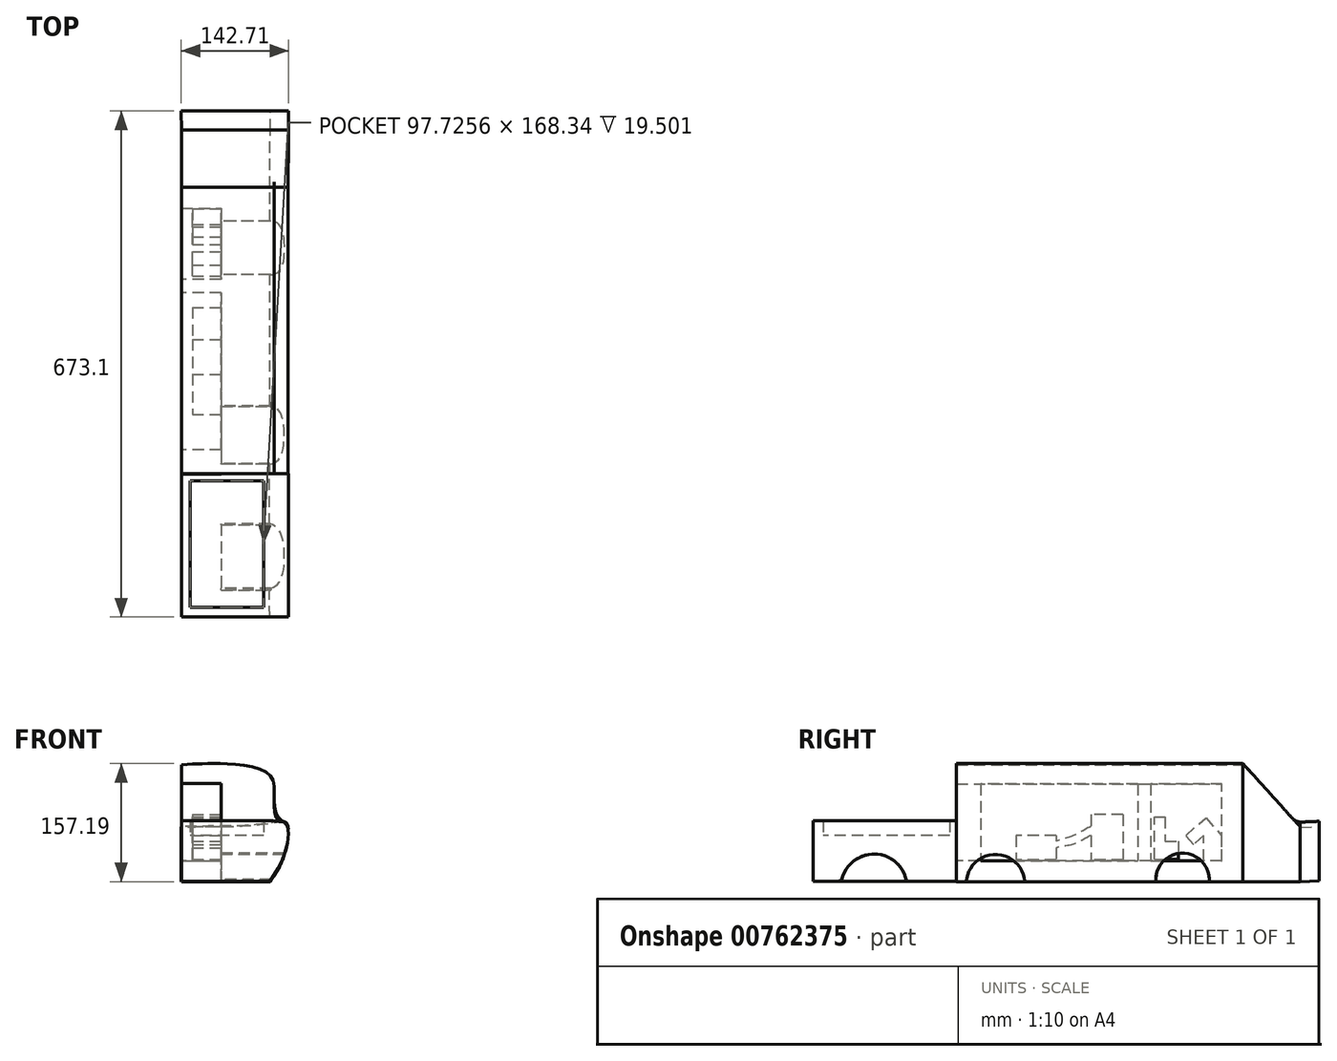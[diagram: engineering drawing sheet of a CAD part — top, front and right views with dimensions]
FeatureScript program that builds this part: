
annotation { "Feature Type Name" : "Feature", "Feature Type Description" : "" }
export const myFeature = defineFeature(function(context is Context, id is Id, definition is map)
    precondition{}
    {
        {
            var Q0;
            Q0=qCreatedBy(makeId("Front.planeOp"),FACE);
            var sketch = newSketch(context, id + "F0", { "sketchPlane" : qUnion([Q0])});
            skLineSegment(sketch, "E0", {"start": v(64.52, -61.5) * mm, "end": v(-52.73, -61.5) * mm});
            skLineSegment(sketch, "E1", {"start": v(-52.73, -61.5) * mm, "end": v(-52.73, 94.1) * mm});
            skFitSpline(sketch, "E2", {"points": [v(64.52, -61.5) * mm, v(82.8, -28.5) * mm, v(86.82, 15.19) * mm, v(75.67, 20.32) * mm, v(70.32, 47.73) * mm, v(64.52, 80.73) * mm, v(12.36, 95) * mm, v(-26.87, 95.44) * mm, v(-52.73, 94.1) * mm], "startDerivative": vector(158.08, 221.6) * mm, "endDerivative": vector(-278.37, -24.2) * mm});
            skSolve(sketch);
        }
        {
            var Q0;
            Q0=qCreatedBy(makeId("Front.planeOp"),FACE);
            cPlane(context, id + "F1", {"entities" : qUnion([Q0]), "cplaneType" : CPlaneType.OFFSET, "offset" : 381 * mm, "width" : 152.4 * mm, "height" : 152.4 * mm});
        }
        {
            var Q0;
            Q0=qCreatedBy(id+"F1.planeOp",FACE);
            var sketch = newSketch(context, id + "F2", { "sketchPlane" : qUnion([Q0])});
            skLineSegment(sketch, "E3", {"start": v(64.52, -61.5) * mm, "end": v(-52.73, -61.5) * mm});
            skLineSegment(sketch, "E4", {"start": v(-52.73, -61.5) * mm, "end": v(-52.73, 94.1) * mm});
            skFitSpline(sketch, "E5", {"points": [v(64.52, -61.5) * mm, v(82.8, -28.5) * mm, v(86.82, 15.19) * mm, v(75.67, 20.32) * mm, v(70.32, 47.73) * mm, v(64.52, 80.73) * mm, v(12.36, 95) * mm, v(-26.87, 95.44) * mm, v(-52.73, 94.1) * mm], "startDerivative": vector(158.08, 221.6) * mm, "endDerivative": vector(-278.37, -24.2) * mm});
            skSolve(sketch);
        }
        {
            var Q0;
            Q0=makeQuery(id+"F2.imprint","IMPRINT",FACE,{"disambiguationData":[TD([[makeQuery(id+"F2.imprint","IMPRINT",EDGE,{"derivedFrom":sQuery(id+"F2.wireOp",EDGE,"E3")}),-1.0]])]});
            var Q1;
            Q1=makeQuery(id+"F0.imprint","IMPRINT",FACE,{"disambiguationData":[TD([[makeQuery(id+"F0.imprint","IMPRINT",EDGE,{"derivedFrom":sQuery(id+"F0.wireOp",EDGE,"E0")}),-1.0]])]});
            loft(context, id + "F3", {"sheetProfilesArray" : [{ "sheetProfileEntities" : qUnion([Q0]) }, { "sheetProfileEntities" : qUnion([Q1]) }]});
        }
        {
            var Q0;
            Q0=qCreatedBy(makeId("Right.planeOp"),FACE);
            var sketch = newSketch(context, id + "F4", { "sketchPlane" : qUnion([Q0])});
            skLineSegment(sketch, "E6", {"start": v(-28.12, -33.37) * mm, "end": v(-28.12, 68.6) * mm});
            skLineSegment(sketch, "E7", {"start": v(-28.12, 68.6) * mm, "end": v(-605.45, 68.6) * mm});
            skLineSegment(sketch, "E8", {"start": v(-605.45, 68.6) * mm, "end": v(-605.45, -33.37) * mm});
            skLineSegment(sketch, "E9", {"start": v(-605.45, -33.37) * mm, "end": v(-28.12, -33.37) * mm});
            skSolve(sketch);
        }
        {
            var Q0;
            Q0 = qSketchRegion(id + "F4", true);
            extrude(context, id + "F5", {"entities" : qUnion([Q0]), "operationType" : NewBodyOperationType.REMOVE, "oppositeDirection" : true, "depth" : 63.5 * mm, "offsetDistance" : 25.4 * mm});
        }
        {
            var Q0;
            Q0=qCreatedBy(id+"F1.planeOp",FACE);
            var sketch = newSketch(context, id + "F6", { "sketchPlane" : qUnion([Q0])});
            skLineSegment(sketch, "E10", {"start": v(64.38, -61.04) * mm, "end": v(-52.72, -61.04) * mm});
            skLineSegment(sketch, "E11", {"start": v(-52.72, -61.04) * mm, "end": v(-52.72, 19.57) * mm});
            skFitSpline(sketch, "E12", {"points": [v(64.38, -61.04) * mm, v(82.8, -28.5) * mm, v(86.82, 15.19) * mm, v(73.24, 18.44) * mm, v(69.12, 19.2) * mm, v(64.38, 19.5) * mm, v(15.3, 19.5) * mm, v(-21.74, 19.36) * mm, v(-52.72, 19.57) * mm], "startDerivative": vector(146.05, 211.77) * mm, "endDerivative": vector(-266.96, 6) * mm});
            skSolve(sketch);
        }
        {
            var Q0;
            Q0=qCreatedBy(id+"F1.planeOp",FACE);
            cPlane(context, id + "F7", {"entities" : qUnion([Q0]), "cplaneType" : CPlaneType.OFFSET, "offset" : 190.5 * mm, "width" : 152.4 * mm, "height" : 152.4 * mm});
        }
        {
            var Q0;
            Q0=qCreatedBy(id+"F7.planeOp",FACE);
            var sketch = newSketch(context, id + "F8", { "sketchPlane" : qUnion([Q0])});
            skLineSegment(sketch, "E13", {"start": v(64.51, -60.9) * mm, "end": v(-52.58, -60.9) * mm});
            skLineSegment(sketch, "E14", {"start": v(-52.58, -60.9) * mm, "end": v(-52.58, 19.7) * mm});
            skFitSpline(sketch, "E15", {"points": [v(64.51, -60.9) * mm, v(82.94, -28.37) * mm, v(86.95, 15.32) * mm, v(73.38, 18.57) * mm, v(69.25, 19.32) * mm, v(64.51, 19.63) * mm, v(15.44, 19.64) * mm, v(-21.6, 19.5) * mm, v(-52.58, 19.7) * mm], "startDerivative": vector(146.05, 211.77) * mm, "endDerivative": vector(-266.96, 6) * mm});
            skSolve(sketch);
        }
        {
            var Q1;
            Q1 = qSketchRegion(id + "F8", true);
            var Q2;
            Q2 = qSketchRegion(id + "F6", true);
            loft(context, id + "F9", {"operationType" : NewBodyOperationType.ADD, "sheetProfilesArray" : [{ "sheetProfileEntities" : qUnion([Q1]) }, { "sheetProfileEntities" : qUnion([Q2]) }]});
        }
        {
            var Q0;
            Q0=qCreatedBy(makeId("Right.planeOp"),FACE);
            var sketch = newSketch(context, id + "F10", { "sketchPlane" : qUnion([Q0])});
            skLineSegment(sketch, "E16.bottom", {"start": v(-381.46, 69.19) * mm, "end": v(-349.12, 69.19) * mm});
            skLineSegment(sketch, "E16.top", {"start": v(-381.46, -33.67) * mm, "end": v(-349.12, -33.67) * mm});
            skLineSegment(sketch, "E16.left", {"start": v(-381.46, 69.19) * mm, "end": v(-381.46, -33.67) * mm});
            skLineSegment(sketch, "E16.right", {"start": v(-349.12, 69.19) * mm, "end": v(-349.12, -33.67) * mm});
            skSolve(sketch);
        }
        {
            var Q0;
            Q0 = qSketchRegion(id + "F10", true);
            extrude(context, id + "F11", {"entities" : qUnion([Q0]), "operationType" : NewBodyOperationType.ADD, "oppositeDirection" : true, "depth" : 52.58 * mm, "offsetDistance" : 25.4 * mm});
        }
        {
            var Q0;
            Q0=qCreatedBy(makeId("Right.planeOp"),FACE);
            var sketch = newSketch(context, id + "F12", { "sketchPlane" : qUnion([Q0])});
            skLineSegment(sketch, "E17.bottom", {"start": v(-122.74, 68.66) * mm, "end": v(-140.23, 68.66) * mm});
            skLineSegment(sketch, "E17.top", {"start": v(-122.74, -33.67) * mm, "end": v(-140.23, -33.67) * mm});
            skLineSegment(sketch, "E17.left", {"start": v(-122.74, 68.66) * mm, "end": v(-122.74, -33.67) * mm});
            skLineSegment(sketch, "E17.right", {"start": v(-140.23, 68.66) * mm, "end": v(-140.23, -33.67) * mm});
            skSolve(sketch);
        }
        {
            var Q0;
            Q0 = qSketchRegion(id + "F12", true);
            extrude(context, id + "F13", {"entities" : qUnion([Q0]), "operationType" : NewBodyOperationType.ADD, "oppositeDirection" : true, "depth" : 52.58 * mm, "offsetDistance" : 25.4 * mm});
        }
        {
            var Q0;
            Q0=qCreatedBy(makeId("Top.planeOp"),FACE);
            var sketch = newSketch(context, id + "F14", { "sketchPlane" : qUnion([Q0])});
            skLineSegment(sketch, "E18.bottom", {"start": v(56.59, -390.26) * mm, "end": v(-41.14, -390.26) * mm});
            skLineSegment(sketch, "E18.top", {"start": v(56.59, -558.6) * mm, "end": v(-41.14, -558.6) * mm});
            skLineSegment(sketch, "E18.left", {"start": v(56.59, -390.26) * mm, "end": v(56.59, -558.6) * mm});
            skLineSegment(sketch, "E18.right", {"start": v(-41.14, -390.26) * mm, "end": v(-41.14, -558.6) * mm});
            skSolve(sketch);
        }
        {
            var Q0;
            Q0 = qSketchRegion(id + "F14", true);
            extrude(context, id + "F15", {"entities" : qUnion([Q0]), "operationType" : NewBodyOperationType.REMOVE, "depth" : 25.4 * mm, "offsetDistance" : 25.4 * mm});
        }
        {
            var Q0;
            Q0=qCreatedBy(makeId("Right.planeOp"),FACE);
            var sketch = newSketch(context, id + "F16", { "sketchPlane" : qUnion([Q0])});
            skArc(sketch, "E19", {"start": v(-45.12, -62.68) * mm, "mid": v(-80.21, -23.36) * mm, "end": v(-115.97, -62.07) * mm});
            skArc(sketch, "E20", {"start": v(-290.39, -60.26) * mm, "mid": v(-329.42, -25.13) * mm, "end": v(-367.9, -60.86) * mm});
            skArc(sketch, "E21", {"start": v(-447.84, -59.65) * mm, "mid": v(-491.09, -24.51) * mm, "end": v(-533.84, -60.26) * mm});
            skLineSegment(sketch, "E22", {"start": v(-533.84, -60.26) * mm, "end": v(-447.84, -59.65) * mm});
            skLineSegment(sketch, "E23", {"start": v(-367.9, -60.86) * mm, "end": v(-290.39, -60.26) * mm});
            skLineSegment(sketch, "E24", {"start": v(-115.97, -62.07) * mm, "end": v(-45.12, -62.68) * mm});
            skSolve(sketch);
        }
        {
            var Q0;
            Q0 = qSketchRegion(id + "F16", true);
            extrude(context, id + "F17", {"entities" : qUnion([Q0]), "operationType" : NewBodyOperationType.REMOVE, "depth" : 88.9 * mm, "offsetDistance" : 25.4 * mm});
        }
        {
            var Q0;
            Q0=qCreatedBy(makeId("Right.planeOp"),FACE);
            var sketch = newSketch(context, id + "F18", { "sketchPlane" : qUnion([Q0])});
            skLineSegment(sketch, "E25.bottom", {"start": v(-535.74, -58.24) * mm, "end": v(-448.6, -58.24) * mm});
            skLineSegment(sketch, "E25.top", {"start": v(-535.74, -68.91) * mm, "end": v(-448.6, -68.91) * mm});
            skLineSegment(sketch, "E25.left", {"start": v(-535.74, -58.24) * mm, "end": v(-535.74, -68.91) * mm});
            skLineSegment(sketch, "E25.right", {"start": v(-448.6, -58.24) * mm, "end": v(-448.6, -68.91) * mm});
            skLineSegment(sketch, "E26.bottom", {"start": v(-367.68, -59.13) * mm, "end": v(-291.21, -59.13) * mm});
            skLineSegment(sketch, "E26.top", {"start": v(-367.68, -76.03) * mm, "end": v(-291.21, -76.03) * mm});
            skLineSegment(sketch, "E26.left", {"start": v(-367.68, -59.13) * mm, "end": v(-367.68, -76.03) * mm});
            skLineSegment(sketch, "E26.right", {"start": v(-291.21, -59.13) * mm, "end": v(-291.21, -76.03) * mm});
            skSolve(sketch);
        }
        {
            var Q0;
            Q0 = qSketchRegion(id + "F18", true);
            extrude(context, id + "F19", {"entities" : qUnion([Q0]), "operationType" : NewBodyOperationType.REMOVE, "depth" : 76.2 * mm, "offsetDistance" : 25.4 * mm});
        }
        {
            var Q0;
            Q0=qCreatedBy(makeId("Right.planeOp"),FACE);
            var sketch = newSketch(context, id + "F20", { "sketchPlane" : qUnion([Q0])});
            skLineSegment(sketch, "E27.bottom", {"start": v(-159.61, 28) * mm, "end": v(-202.3, 28) * mm});
            skLineSegment(sketch, "E27.top", {"start": v(-159.61, -32.46) * mm, "end": v(-202.3, -32.46) * mm});
            skLineSegment(sketch, "E27.left", {"start": v(-159.61, 28) * mm, "end": v(-159.61, -32.46) * mm});
            skLineSegment(sketch, "E27.right", {"start": v(-202.3, 28) * mm, "end": v(-202.3, -32.46) * mm});
            skLineSegment(sketch, "E28.bottom", {"start": v(-248.53, 0) * mm, "end": v(-301.88, 0) * mm});
            skLineSegment(sketch, "E28.top", {"start": v(-248.53, -32.46) * mm, "end": v(-301.88, -32.46) * mm});
            skLineSegment(sketch, "E28.left", {"start": v(-248.53, 0) * mm, "end": v(-248.53, -32.46) * mm});
            skLineSegment(sketch, "E28.right", {"start": v(-301.88, 0) * mm, "end": v(-301.88, -32.46) * mm});
            skFitSpline(sketch, "E29", {"points": [v(-202.3, 12) * mm, v(-225.41, 0) * mm, v(-248.53, -7.56) * mm], "startDerivative": vector(-49.58, -24.2) * mm, "endDerivative": vector(-42.75, -14.72) * mm});
            skFitSpline(sketch, "E30", {"points": [v(-202.3, 0) * mm, v(-223.63, -11.12) * mm, v(-248.53, -16.23) * mm], "startDerivative": vector(-44.18, -20.12) * mm, "endDerivative": vector(-48.29, -12.36) * mm});
            skSolve(sketch);
        }
        {
            var Q0;
            Q0 = qSketchRegion(id + "F20", true);
            extrude(context, id + "F21", {"entities" : qUnion([Q0]), "operationType" : NewBodyOperationType.ADD, "oppositeDirection" : true, "depth" : 38.1 * mm, "offsetDistance" : 25.4 * mm});
        }
        {
            var Q0;
            Q0=qCreatedBy(makeId("Right.planeOp"),FACE);
            var sketch = newSketch(context, id + "F22", { "sketchPlane" : qUnion([Q0])});
            skLineSegment(sketch, "E31", {"start": v(-117.82, -31.57) * mm, "end": v(-117.82, 24.45) * mm});
            skLineSegment(sketch, "E32", {"start": v(-117.82, 24.45) * mm, "end": v(-103.6, 24.45) * mm});
            skLineSegment(sketch, "E33", {"start": v(-103.6, 24.45) * mm, "end": v(-103.6, -7.56) * mm});
            skLineSegment(sketch, "E34", {"start": v(-103.6, -7.56) * mm, "end": v(-85.8, -7.56) * mm});
            skLineSegment(sketch, "E35", {"start": v(-85.8, -7.56) * mm, "end": v(-85.8, -31.57) * mm});
            skLineSegment(sketch, "E36", {"start": v(-117.82, -31.57) * mm, "end": v(-85.8, -31.57) * mm});
            skSolve(sketch);
        }
        {
            var Q0;
            Q0 = qSketchRegion(id + "F22", true);
            extrude(context, id + "F23", {"entities" : qUnion([Q0]), "operationType" : NewBodyOperationType.ADD, "oppositeDirection" : true, "depth" : 38.1 * mm, "offsetDistance" : 25.4 * mm});
        }
        {
            var Q0;
            Q0=qCreatedBy(makeId("Right.planeOp"),FACE);
            var sketch = newSketch(context, id + "F24", { "sketchPlane" : qUnion([Q0])});
            skLineSegment(sketch, "E37", {"start": v(-52.36, -34.1) * mm, "end": v(-52.36, 0) * mm});
            skLineSegment(sketch, "E38", {"start": v(-52.36, 0) * mm, "end": v(-65.71, -11.75) * mm});
            skLineSegment(sketch, "E39", {"start": v(-65.71, -11.75) * mm, "end": v(-76.05, 0) * mm});
            skLineSegment(sketch, "E40", {"start": v(-76.05, 0) * mm, "end": v(-49.41, 23.44) * mm});
            skLineSegment(sketch, "E41", {"start": v(-49.41, 23.44) * mm, "end": v(-28.79, 0) * mm});
            skLineSegment(sketch, "E42", {"start": v(-28.79, 0) * mm, "end": v(-28.79, -34.09) * mm});
            skLineSegment(sketch, "E43", {"start": v(-28.79, -34.09) * mm, "end": v(-52.36, -34.1) * mm});
            skSolve(sketch);
        }
        {
            var Q0;
            Q0 = qSketchRegion(id + "F24", true);
            extrude(context, id + "F25", {"entities" : qUnion([Q0]), "operationType" : NewBodyOperationType.ADD, "oppositeDirection" : true, "depth" : 38.1 * mm, "offsetDistance" : 25.4 * mm});
        }
        {
            var Q0;
            Q0=qCreatedBy(makeId("Front.planeOp"),FACE);
            cPlane(context, id + "F26", {"entities" : qUnion([Q0]), "cplaneType" : CPlaneType.OFFSET, "offset" : 76.2 * mm, "oppositeDirection" : true, "width" : 152.4 * mm, "height" : 152.4 * mm});
        }
        {
            var Q0;
            Q0=qCreatedBy(id+"F26.planeOp",FACE);
            var sketch = newSketch(context, id + "F27", { "sketchPlane" : qUnion([Q0])});
            skLineSegment(sketch, "E44", {"start": v(65.22, -61.38) * mm, "end": v(-52.93, -61.38) * mm});
            skLineSegment(sketch, "E45", {"start": v(-52.93, -61.38) * mm, "end": v(-52.93, 10.5) * mm});
            skFitSpline(sketch, "E46", {"points": [v(65.22, -61.38) * mm, v(83.22, -28.53) * mm, v(87.3, 15.18) * mm, v(75.84, 17.3) * mm, v(65.22, 15.4) * mm, v(24.11, 11.86) * mm, v(-19.45, 11.31) * mm, v(-52.93, 10.5) * mm], "startDerivative": vector(155.68, 231.32) * mm, "endDerivative": vector(-230.58, -5.76) * mm});
            skSolve(sketch);
        }
        {
            var Q1;
            Q1=makeQuery(id+"F3.opLoft","CAP_FACE",FACE,{"disambiguationData":[OSD([makeQuery(id+"F0.imprint","IMPRINT",FACE,{"disambiguationData":[TD([[makeQuery(id+"F0.imprint","IMPRINT",EDGE,{"derivedFrom":sQuery(id+"F0.wireOp",EDGE,"E0")}),-1.0]])]})])],"isStart":true});
            var Q2;
            Q2=makeQuery(id+"F27.imprint","IMPRINT",FACE,{"disambiguationData":[TD([[makeQuery(id+"F27.imprint","IMPRINT",EDGE,{"derivedFrom":sQuery(id+"F27.wireOp",EDGE,"E44")}),-1.0]])]});
            loft(context, id + "F28", {"operationType" : NewBodyOperationType.ADD, "sheetProfilesArray" : [{ "sheetProfileEntities" : qUnion([Q1]) }, { "sheetProfileEntities" : qUnion([Q2]) }]});
        }
        {
            var Q0;
            Q0=qCreatedBy(id+"F26.planeOp",FACE);
            cPlane(context, id + "F29", {"entities" : qUnion([Q0]), "cplaneType" : CPlaneType.OFFSET, "offset" : 25.4 * mm, "oppositeDirection" : true, "width" : 152.4 * mm, "height" : 152.4 * mm});
        }
        {
            var Q0;
            Q0=qCreatedBy(id+"F29.planeOp",FACE);
            var sketch = newSketch(context, id + "F30", { "sketchPlane" : qUnion([Q0])});
            skLineSegment(sketch, "E47", {"start": v(65.18, -60.28) * mm, "end": v(-52.97, -60.28) * mm});
            skLineSegment(sketch, "E48", {"start": v(-52.97, -60.28) * mm, "end": v(-52.97, 11.6) * mm});
            skFitSpline(sketch, "E49", {"points": [v(65.18, -60.28) * mm, v(83.19, -27.44) * mm, v(87.26, 16.28) * mm, v(75.8, 18.4) * mm, v(65.18, 16.5) * mm, v(24.07, 12.95) * mm, v(-19.49, 12.4) * mm, v(-52.97, 11.6) * mm], "startDerivative": vector(155.68, 231.32) * mm, "endDerivative": vector(-230.58, -5.76) * mm});
            skSolve(sketch);
        }
        {
            var Q1;
            Q1=makeQuery(id+"F28.opLoft","CAP_FACE",FACE,{"disambiguationData":[OSD([makeQuery(id+"F27.imprint","IMPRINT",FACE,{"disambiguationData":[TD([[makeQuery(id+"F27.imprint","IMPRINT",EDGE,{"derivedFrom":sQuery(id+"F27.wireOp",EDGE,"E44")}),-1.0]])]})])],"isStart":true});
            var Q2;
            Q2=makeQuery(id+"F30.imprint","IMPRINT",FACE,{"disambiguationData":[TD([[makeQuery(id+"F30.imprint","IMPRINT",EDGE,{"derivedFrom":sQuery(id+"F30.wireOp",EDGE,"E47")}),-1.0]])]});
            loft(context, id + "F31", {"operationType" : NewBodyOperationType.ADD, "sheetProfilesArray" : [{ "sheetProfileEntities" : qUnion([Q1]) }, { "sheetProfileEntities" : qUnion([Q2]) }]});
        }
    });
